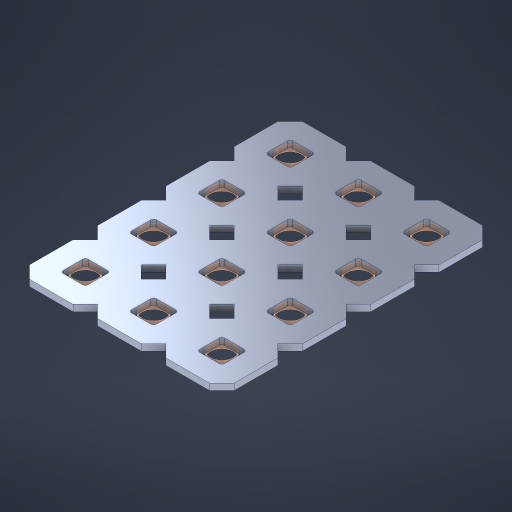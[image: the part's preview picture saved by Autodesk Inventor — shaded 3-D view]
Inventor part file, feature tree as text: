
AUTODESK INVENTOR PART (.ipt)
format: ipt  version: 2023 (Build 270158000, 158)  size: 389,632 bytes
history: native  units: in
note: dims shown in document units (in); Inventor stores cm internally (conversion verified against a paired STEP export)
features: other x13, extrude x11, sketch x2, pattern_linear x1
ambient origin geometry x8: Origin, YZ Plane, XZ Plane, XY Plane, X Axis, Y Axis, Z Axis, Center Point
bodies: Solid1 (feature_tree), Body (feature_tree)
feature tree (27):
  pattern_linear  "Rectangular Pattern1"  Spacing1=0.09in  [1 undecoded]
  sketch  "Sketch1"  dims[d1=0.5in]
  sketch  "Sketch2"  dims[d2=0.182in d3=0.09in d4=0.09in d5=0.09in d6=0.09in d7=0.09in d8=0.09in d9=0.09in d10=0.09in d11=0.02in d13=0.0in d14=0.172in d15=0.0625in d16=0.0in d19=0.5in d22=0.5in]
  other  "Srf1"
  other  "Srf126"
  other  "Srf127"
  other  "Srf128"
  other  "Srf268"
  other  "Srf269"
  other  "Srf270"
  other  "Srf271"
  other  "Srf293"
  other  "Srf294"
  other  "Srf295"
  other  "Srf296"
  other  "Circle"
  extrude  "ExtrusionSrf126"  Depth=0.09in
  extrude  "ExtrusionSrf127"  Depth=0.09in
  extrude  "ExtrusionSrf128"  Depth=0.09in
  extrude  "ExtrusionSrf268"  Depth=0.09in
  extrude  "ExtrusionSrf269"  Depth=0.09in
  extrude  "ExtrusionSrf270"  Depth=0.09in
  extrude  "ExtrusionSrf271"  Depth=0.09in
  extrude  "ExtrusionSrf293"  Depth=0.02in
  extrude  "ExtrusionSrf294"  TaperAngle=0.0deg  [1 undecoded]
  extrude  "ExtrusionSrf295"  Depth=0.5in
  extrude  "ExtrusionSrf296"  Depth=0.5in TaperAngle=0.0deg
note: 2 required parameter values undecoded (feature->parameter linkage not recoverable at this tier; creation-order binding heuristic only, values carry confidence <= 0.55)
